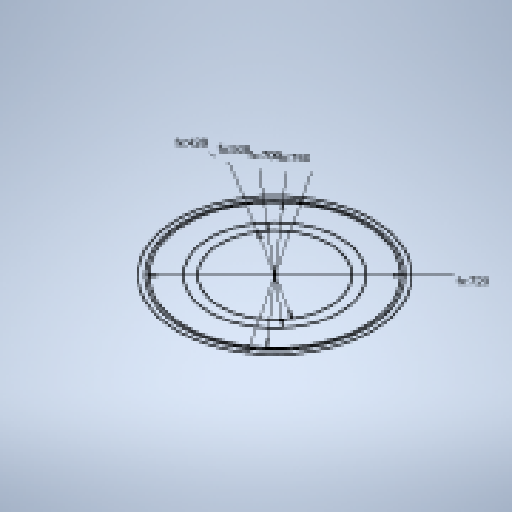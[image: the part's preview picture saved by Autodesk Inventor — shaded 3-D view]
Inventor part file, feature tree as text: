
AUTODESK INVENTOR PART (.ipt)
format: ipt  version: 2025 (Build 290162010, 162A)  size: 152,576 bytes
history: native  units: mm
features: sketch x1
ambient origin geometry x8: Origin, YZ Plane, XZ Plane, XY Plane, X Axis, Y Axis, Z Axis, Center Point
feature tree (1):
  sketch  "Sketch1"  dims[d2=720.0mm d3=760.0mm d4=700.0mm d5=508.0mm d6=428.0mm]
